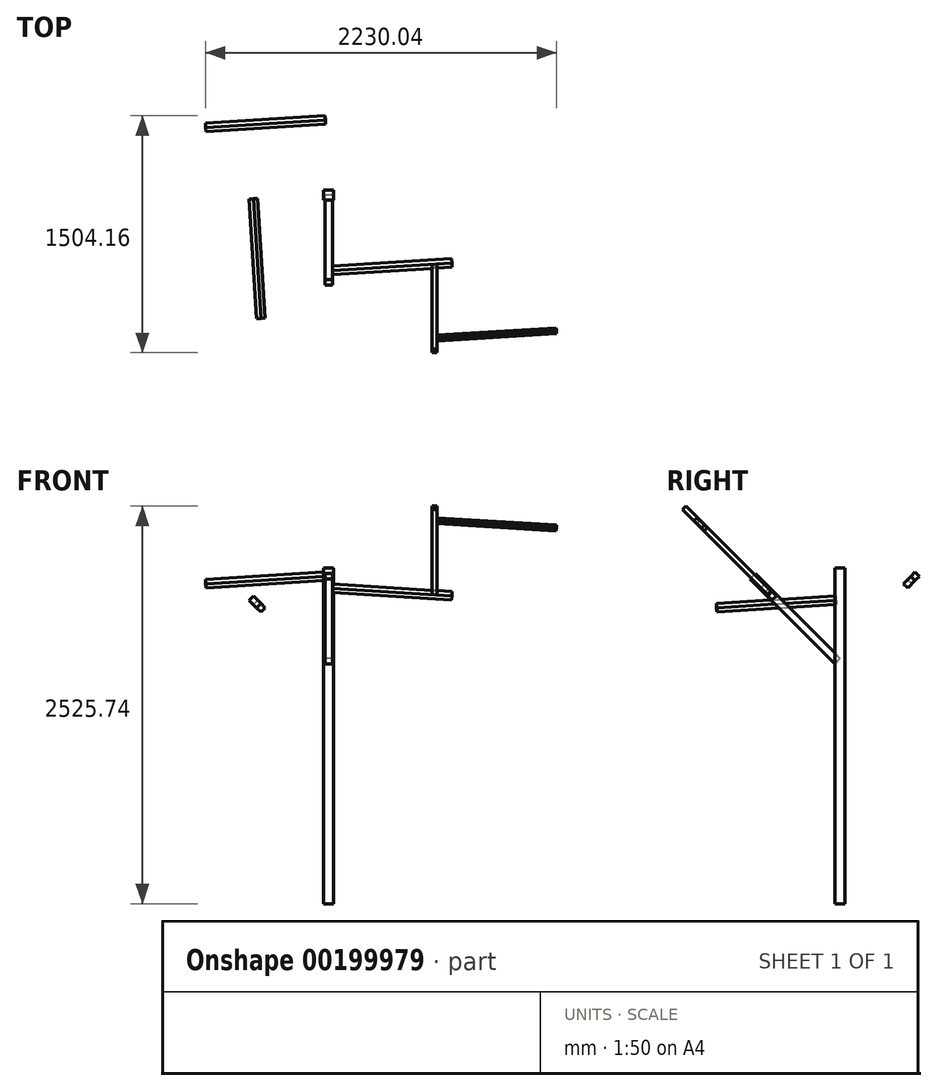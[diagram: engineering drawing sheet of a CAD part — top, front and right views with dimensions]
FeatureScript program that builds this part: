
annotation { "Feature Type Name" : "Feature", "Feature Type Description" : "" }
export const myFeature = defineFeature(function(context is Context, id is Id, definition is map)
    precondition{}
    {
        {
            assignVariable(context, id + "F0", {"name" : "H", "anyValue" : 2133.6 * mm});
        }
        {
            assignVariable(context, id + "F1", {"name" : "L1", "anyValue" : 762 * mm});
        }
        {
            var Q0;
            Q0=qCreatedBy(makeId("Top.planeOp"),FACE);
            var sketch = newSketch(context, id + "F2", { "sketchPlane" : qUnion([Q0])});
            skLineSegment(sketch, "E0.bottom", {"start": v(31.75, 31.75) * mm, "end": v(-31.75, 31.75) * mm});
            skLineSegment(sketch, "E0.top", {"start": v(31.75, -31.75) * mm, "end": v(-31.75, -31.75) * mm});
            skLineSegment(sketch, "E0.left", {"start": v(31.75, 31.75) * mm, "end": v(31.75, -31.75) * mm});
            skLineSegment(sketch, "E0.right", {"start": v(-31.75, 31.75) * mm, "end": v(-31.75, -31.75) * mm});
            skPoint(sketch, "E0.middle", {"position": v(0, 0) * mm});
            skSolve(sketch);
        }
        {
            var Q0;
            Q0=makeQuery(id+"F2.imprint","IMPRINT",FACE,{"disambiguationData":[TD([[makeQuery(id+"F2.imprint","IMPRINT",EDGE,{"derivedFrom":sQuery(id+"F2.wireOp",EDGE,"E0.bottom")}),1.0]])]});
            extrude(context, id + "F3", {"entities" : qUnion([Q0]), "depth" : getVariable(context, 'H')});
        }
        {
            var Q0;
            Q0=makeQuery(id+"F3.opExtrude","SWEPT_FACE",FACE,{"disambiguationData":[OSD([sQuery(id+"F2.wireOp",EDGE,"E0.top")])]});
            var sketch = newSketch(context, id + "F4", { "sketchPlane" : qUnion([Q0])});
            skLineSegment(sketch, "E1.bottom", {"start": v(23.81, 1571.62) * mm, "end": v(-23.81, 1571.62) * mm});
            skLineSegment(sketch, "E1.top", {"start": v(23.81, 1524) * mm, "end": v(-23.81, 1524) * mm});
            skLineSegment(sketch, "E1.left", {"start": v(23.81, 1571.62) * mm, "end": v(23.81, 1524) * mm});
            skLineSegment(sketch, "E1.right", {"start": v(-23.81, 1571.62) * mm, "end": v(-23.81, 1524) * mm});
            skPoint(sketch, "E1.middle", {"position": v(0, 1547.81) * mm});
            skPoint(sketch, "E1.middle.positionSnap0", {"position": v(0, 0) * mm});
            skPoint(sketch, "E1.centerSnap0", {"position": v(0, 0) * mm});
            skSolve(sketch);
        }
        {
            var Q0;
            Q0=makeQuery(id+"F4.imprint","IMPRINT",FACE,{"disambiguationData":[TD([[makeQuery(id+"F4.imprint","IMPRINT",EDGE,{"derivedFrom":sQuery(id+"F4.wireOp",EDGE,"E1.bottom")}),1.0]])]});
            extrude(context, id + "F5", {"entities" : qUnion([Q0]), "depth" : getVariable(context, 'L1')});
        }
        {
            var Q0;
            Q0=makeQuery(id+"F5.opExtrude","SWEPT_FACE",FACE,{"disambiguationData":[OSD([sQuery(id+"F4.wireOp",EDGE,"E1.left")])]});
            var sketch = newSketch(context, id + "F6", { "sketchPlane" : qUnion([Q0])});
            skLineSegment(sketch, "E2.bottom", {"start": v(-666.75, 1566.86) * mm, "end": v(-704.85, 1566.86) * mm});
            skLineSegment(sketch, "E2.top", {"start": v(-666.75, 1528.76) * mm, "end": v(-704.85, 1528.76) * mm});
            skLineSegment(sketch, "E2.left", {"start": v(-666.75, 1566.86) * mm, "end": v(-666.75, 1528.76) * mm});
            skLineSegment(sketch, "E2.right", {"start": v(-704.85, 1566.86) * mm, "end": v(-704.85, 1528.76) * mm});
            skPoint(sketch, "E2.middle", {"position": v(-685.8, 1547.81) * mm});
            skPoint(sketch, "E2.middle.positionSnap0", {"position": v(-793.75, 1547.81) * mm});
            skPoint(sketch, "E2.centerSnap0", {"position": v(-793.75, 1547.81) * mm});
            skSolve(sketch);
        }
        {
            var Q0;
            Q0=makeQuery(id+"F6.imprint","IMPRINT",FACE,{"disambiguationData":[TD([[makeQuery(id+"F6.imprint","IMPRINT",EDGE,{"derivedFrom":sQuery(id+"F6.wireOp",EDGE,"E2.bottom")}),1.0]])]});
            extrude(context, id + "F7", {"entities" : qUnion([Q0]), "depth" : getVariable(context, 'L1')});
        }
        {
            var Q0;
            Q0=makeQuery(id+"F7.opExtrude","SWEPT_FACE",FACE,{"disambiguationData":[OSD([sQuery(id+"F6.wireOp",EDGE,"E2.right")])]});
            var sketch = newSketch(context, id + "F8", { "sketchPlane" : qUnion([Q0])});
            skLineSegment(sketch, "E3.bottom", {"start": v(690.56, 1563.69) * mm, "end": v(658.81, 1563.69) * mm});
            skLineSegment(sketch, "E3.top", {"start": v(690.56, 1531.94) * mm, "end": v(658.81, 1531.94) * mm});
            skLineSegment(sketch, "E3.left", {"start": v(690.56, 1563.69) * mm, "end": v(690.56, 1531.94) * mm});
            skLineSegment(sketch, "E3.right", {"start": v(658.81, 1563.69) * mm, "end": v(658.81, 1531.94) * mm});
            skPoint(sketch, "E3.middle", {"position": v(674.69, 1547.81) * mm});
            skPoint(sketch, "E3.middle.positionSnap0", {"position": v(785.81, 1547.81) * mm});
            skPoint(sketch, "E3.centerSnap0", {"position": v(785.81, 1547.81) * mm});
            skSolve(sketch);
        }
        {
            var Q0;
            Q0=makeQuery(id+"F8.imprint","IMPRINT",FACE,{"disambiguationData":[TD([[makeQuery(id+"F8.imprint","IMPRINT",EDGE,{"derivedFrom":sQuery(id+"F8.wireOp",EDGE,"E3.bottom")}),1.0]])]});
            extrude(context, id + "F9", {"entities" : qUnion([Q0]), "depth" : getVariable(context, 'L1')});
        }
        {
            var Q0;
            Q0=makeQuery(id+"F9.opExtrude","SWEPT_FACE",FACE,{"disambiguationData":[OSD([sQuery(id+"F8.wireOp",EDGE,"E3.left")])]});
            var sketch = newSketch(context, id + "F10", { "sketchPlane" : qUnion([Q0])});
            skLineSegment(sketch, "E4.bottom", {"start": v(-1339.85, 1560.51) * mm, "end": v(-1365.25, 1560.51) * mm});
            skLineSegment(sketch, "E4.top", {"start": v(-1339.85, 1535.11) * mm, "end": v(-1365.25, 1535.11) * mm});
            skLineSegment(sketch, "E4.left", {"start": v(-1339.85, 1560.51) * mm, "end": v(-1339.85, 1535.11) * mm});
            skLineSegment(sketch, "E4.right", {"start": v(-1365.25, 1560.51) * mm, "end": v(-1365.25, 1535.11) * mm});
            skPoint(sketch, "E4.middle", {"position": v(-1352.55, 1547.81) * mm});
            skPoint(sketch, "E4.middle.positionSnap0", {"position": v(-1466.85, 1547.81) * mm});
            skPoint(sketch, "E4.centerSnap0", {"position": v(-1466.85, 1547.81) * mm});
            skSolve(sketch);
        }
        {
            var Q0;
            Q0=makeQuery(id+"F10.imprint","IMPRINT",FACE,{"disambiguationData":[TD([[makeQuery(id+"F10.imprint","IMPRINT",EDGE,{"derivedFrom":sQuery(id+"F10.wireOp",EDGE,"E4.bottom")}),1.0]])]});
            extrude(context, id + "F11", {"entities" : qUnion([Q0]), "depth" : getVariable(context, 'L1')});
        }
        {
            var Q0;
            Q0=makeQuery(id+"F7.opExtrude","SWEPT_BODY",BODY,{"disambiguationData":[OSD([sQuery(id+"F6.wireOp",EDGE,"E2.bottom"),sQuery(id+"F6.wireOp",EDGE,"E2.top"),sQuery(id+"F6.wireOp",EDGE,"E2.left"),sQuery(id+"F6.wireOp",EDGE,"E2.right")])]});
            var Q1;
            Q1=makeQuery(id+"F9.opExtrude","SWEPT_BODY",BODY,{"disambiguationData":[OSD([sQuery(id+"F8.wireOp",EDGE,"E3.bottom"),sQuery(id+"F8.wireOp",EDGE,"E3.top"),sQuery(id+"F8.wireOp",EDGE,"E3.left"),sQuery(id+"F8.wireOp",EDGE,"E3.right")])]});
            var Q2;
            Q2=makeQuery(id+"F5.opExtrude","SWEPT_BODY",BODY,{"disambiguationData":[OSD([sQuery(id+"F4.wireOp",EDGE,"E1.bottom"),sQuery(id+"F4.wireOp",EDGE,"E1.top"),sQuery(id+"F4.wireOp",EDGE,"E1.left"),sQuery(id+"F4.wireOp",EDGE,"E1.right")])]});
            var Q3;
            Q3=makeQuery(id+"F11.opExtrude","SWEPT_BODY",BODY,{"disambiguationData":[OSD([sQuery(id+"F10.wireOp",EDGE,"E4.bottom"),sQuery(id+"F10.wireOp",EDGE,"E4.top"),sQuery(id+"F10.wireOp",EDGE,"E4.left"),sQuery(id+"F10.wireOp",EDGE,"E4.right")])]});
            var Q4;
            Q4=makeQuery(id+"F5.opExtrude","CAP_EDGE",EDGE,{"disambiguationData":[OSD([sQuery(id+"F4.wireOp",EDGE,"E1.top")])],"isStart":true});
            transform(context, id + "F12", {"entities" : qUnion([Q0, Q1, Q2, Q3]), "transformType" : TransformType.ROTATION, "transformAxis" : qUnion([Q4]), "angle" : 45 * degree, "makeCopy" : false});
        }
        {
            var Q0;
            Q0=makeQuery(id+"F7.opExtrude","SWEPT_BODY",BODY,{"disambiguationData":[OSD([sQuery(id+"F6.wireOp",EDGE,"E2.bottom"),sQuery(id+"F6.wireOp",EDGE,"E2.top"),sQuery(id+"F6.wireOp",EDGE,"E2.left"),sQuery(id+"F6.wireOp",EDGE,"E2.right")])]});
            var Q1;
            Q1=makeQuery(id+"F9.opExtrude","SWEPT_BODY",BODY,{"disambiguationData":[OSD([sQuery(id+"F8.wireOp",EDGE,"E3.bottom"),sQuery(id+"F8.wireOp",EDGE,"E3.top"),sQuery(id+"F8.wireOp",EDGE,"E3.left"),sQuery(id+"F8.wireOp",EDGE,"E3.right")])]});
            var Q2;
            Q2=makeQuery(id+"F11.opExtrude","SWEPT_BODY",BODY,{"disambiguationData":[OSD([sQuery(id+"F10.wireOp",EDGE,"E4.bottom"),sQuery(id+"F10.wireOp",EDGE,"E4.top"),sQuery(id+"F10.wireOp",EDGE,"E4.left"),sQuery(id+"F10.wireOp",EDGE,"E4.right")])]});
            var Q3;
            Q3=makeQuery(id+"F7.opExtrude","CAP_EDGE",EDGE,{"disambiguationData":[OSD([sQuery(id+"F6.wireOp",EDGE,"E2.right")])],"isStart":true});
            transform(context, id + "F13", {"entities" : qUnion([Q0, Q1, Q2]), "transformType" : TransformType.ROTATION, "transformAxis" : qUnion([Q3]), "angle" : 5 * degree, "oppositeDirection" : true, "makeCopy" : false});
        }
        {
            var Q0;
            Q0=makeQuery(id+"F9.opExtrude","SWEPT_BODY",BODY,{"disambiguationData":[OSD([sQuery(id+"F8.wireOp",EDGE,"E3.bottom"),sQuery(id+"F8.wireOp",EDGE,"E3.top"),sQuery(id+"F8.wireOp",EDGE,"E3.left"),sQuery(id+"F8.wireOp",EDGE,"E3.right")])]});
            var Q1;
            Q1=makeQuery(id+"F11.opExtrude","SWEPT_BODY",BODY,{"disambiguationData":[OSD([sQuery(id+"F10.wireOp",EDGE,"E4.bottom"),sQuery(id+"F10.wireOp",EDGE,"E4.top"),sQuery(id+"F10.wireOp",EDGE,"E4.left"),sQuery(id+"F10.wireOp",EDGE,"E4.right")])]});
            var Q2;
            Q2=makeQuery(id+"F9.opExtrude","CAP_EDGE",EDGE,{"disambiguationData":[OSD([sQuery(id+"F8.wireOp",EDGE,"E3.left")])],"isStart":true});
            transform(context, id + "F14", {"entities" : qUnion([Q0, Q1]), "transformType" : TransformType.ROTATION, "transformAxis" : qUnion([Q2]), "angle" : 5 * degree, "makeCopy" : false});
        }
        {
            var Q0;
            Q0=makeQuery(id+"F11.opExtrude","SWEPT_BODY",BODY,{"disambiguationData":[OSD([sQuery(id+"F10.wireOp",EDGE,"E4.bottom"),sQuery(id+"F10.wireOp",EDGE,"E4.top"),sQuery(id+"F10.wireOp",EDGE,"E4.left"),sQuery(id+"F10.wireOp",EDGE,"E4.right")])]});
            var Q1;
            Q1=makeQuery(id+"F11.opExtrude","CAP_EDGE",EDGE,{"disambiguationData":[OSD([sQuery(id+"F10.wireOp",EDGE,"E4.right")])],"isStart":true});
            transform(context, id + "F15", {"entities" : qUnion([Q0]), "transformType" : TransformType.ROTATION, "transformAxis" : qUnion([Q1]), "angle" : 5 * degree, "oppositeDirection" : true, "makeCopy" : false});
        }
        {
            var Q0;
            Q0=qCreatedBy(makeId("Front.planeOp"),FACE);
            var sketch = newSketch(context, id + "F16", { "sketchPlane" : qUnion([Q0])});
            skLineSegment(sketch, "E5", {"start": v(0, 0) * mm, "end": v(0, -67.57) * mm, "construction": true});
            skSolve(sketch);
        }
        {
            var Q0;
            Q0=makeQuery(id+"F7.opExtrude","SWEPT_BODY",BODY,{"disambiguationData":[OSD([sQuery(id+"F6.wireOp",EDGE,"E2.bottom"),sQuery(id+"F6.wireOp",EDGE,"E2.top"),sQuery(id+"F6.wireOp",EDGE,"E2.left"),sQuery(id+"F6.wireOp",EDGE,"E2.right")])]});
            var Q1;
            Q1=sQuery(id+"F16.wireOp",EDGE,"E5");
            circularPattern(context, id + "F17", {"entities" : qUnion([Q0]), "axis" : qUnion([Q1]), "angle" : 180 * degree, "instanceCount" : 3, "equalSpace" : true});
        }
        {
            var Q0;
            Q0=makeQuery(id+"F17.opPattern","COPY",BODY,{"derivedFrom":makeQuery(id+"F7.opExtrude","SWEPT_BODY",BODY,{"disambiguationData":[OSD([sQuery(id+"F6.wireOp",EDGE,"E2.bottom"),sQuery(id+"F6.wireOp",EDGE,"E2.top"),sQuery(id+"F6.wireOp",EDGE,"E2.left"),sQuery(id+"F6.wireOp",EDGE,"E2.right")])]}),"instanceName":"1"});
            var Q1;
            Q1=makeQuery(id+"F3.opExtrude","SWEPT_EDGE",EDGE,{"disambiguationData":[OSD([sQuery(id+"F2.wireOp",EDGE,"E0.top"),sQuery(id+"F2.wireOp",EDGE,"E0.right")])]});
            transform(context, id + "F18", {"entities" : qUnion([Q0]), "transformType" : TransformType.TRANSLATION_3D, "dx" : 0 * mm, "dy" : 0 * mm, "dz" : -76.2 * mm, "makeCopy" : false});
        }
        {
            var Q0;
            Q0=makeQuery(id+"F17.opPattern","COPY",BODY,{"derivedFrom":makeQuery(id+"F7.opExtrude","SWEPT_BODY",BODY,{"disambiguationData":[OSD([sQuery(id+"F6.wireOp",EDGE,"E2.bottom"),sQuery(id+"F6.wireOp",EDGE,"E2.top"),sQuery(id+"F6.wireOp",EDGE,"E2.left"),sQuery(id+"F6.wireOp",EDGE,"E2.right")])]}),"instanceName":"2"});
            transform(context, id + "F19", {"entities" : qUnion([Q0]), "transformType" : TransformType.TRANSLATION_3D, "dx" : 0 * mm, "dy" : 0 * mm, "dz" : 76.2 * mm, "makeCopy" : false});
        }
    });
